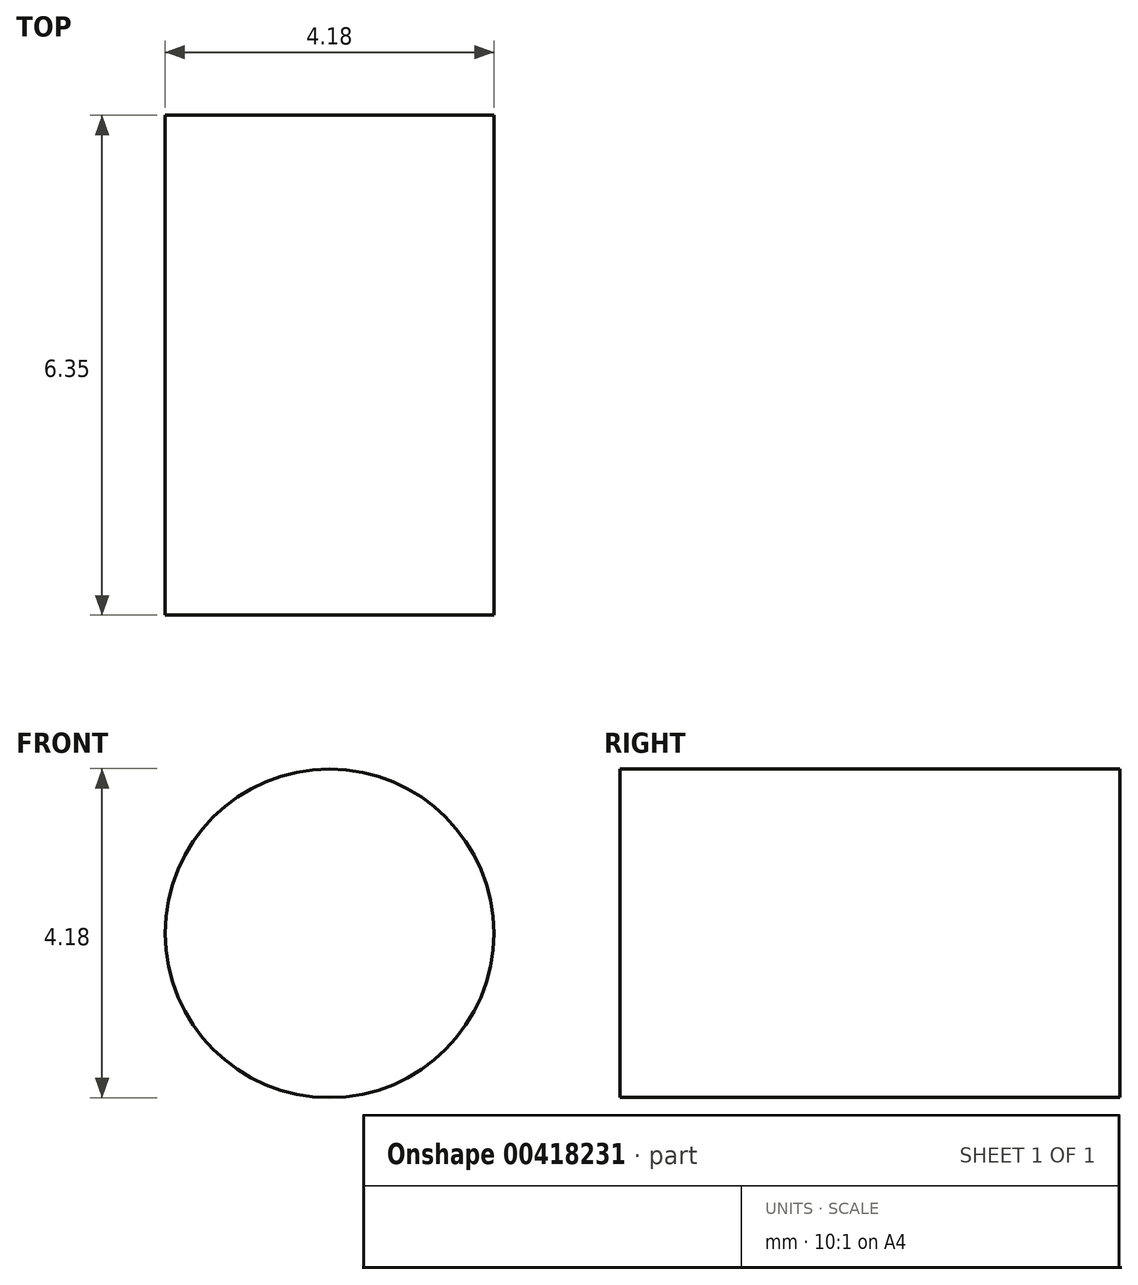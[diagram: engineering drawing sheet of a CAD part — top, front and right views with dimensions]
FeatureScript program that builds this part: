
annotation { "Feature Type Name" : "Feature", "Feature Type Description" : "" }
export const myFeature = defineFeature(function(context is Context, id is Id, definition is map)
    precondition{}
    {
        {
            var Q0;
            Q0=qCreatedBy(makeId("Front.planeOp"),FACE);
            var sketch = newSketch(context, id + "F0", { "sketchPlane" : qUnion([Q0])});
            skCircle(sketch, "E0", {"center": v(-3.16, 0) * mm, "radius": 2.09 * mm});
            skPoint(sketch, "E0.first.point", {"position": v(-2.43, -1.95) * mm});
            skPoint(sketch, "E0.second.point", {"position": v(-3.9, 1.96) * mm});
            skPoint(sketch, "E0.third.point", {"position": v(-1.22, 0.78) * mm});
            skLineSegment(sketch, "E1", {"start": v(0, 0) * mm, "end": v(0, 1.44) * mm});
            skCircle(sketch, "E2.MirrorC", {"center": v(3.16, 0) * mm, "radius": 2.09 * mm});
            skSolve(sketch);
        }
        {
            var Q0;
            Q0=makeQuery(id+"F0.imprint","IMPRINT",FACE,{"disambiguationData":[TD([[makeQuery(id+"F0.imprint","IMPRINT",EDGE,{"derivedFrom":sQuery(id+"F0.wireOp",EDGE,"E0")}),1.0]])]});
            var Q1;
            Q1=makeQuery(id+"F0.imprint","IMPRINT",FACE,{"disambiguationData":[TD([[makeQuery(id+"F0.imprint","IMPRINT",EDGE,{"derivedFrom":sQuery(id+"F0.wireOp",EDGE,"E2.MirrorC")}),-1.0]])]});
            extrude(context, id + "F1", {"entities" : qUnion([Q0, Q1]), "depth" : 6.35 * mm});
        }
    });
